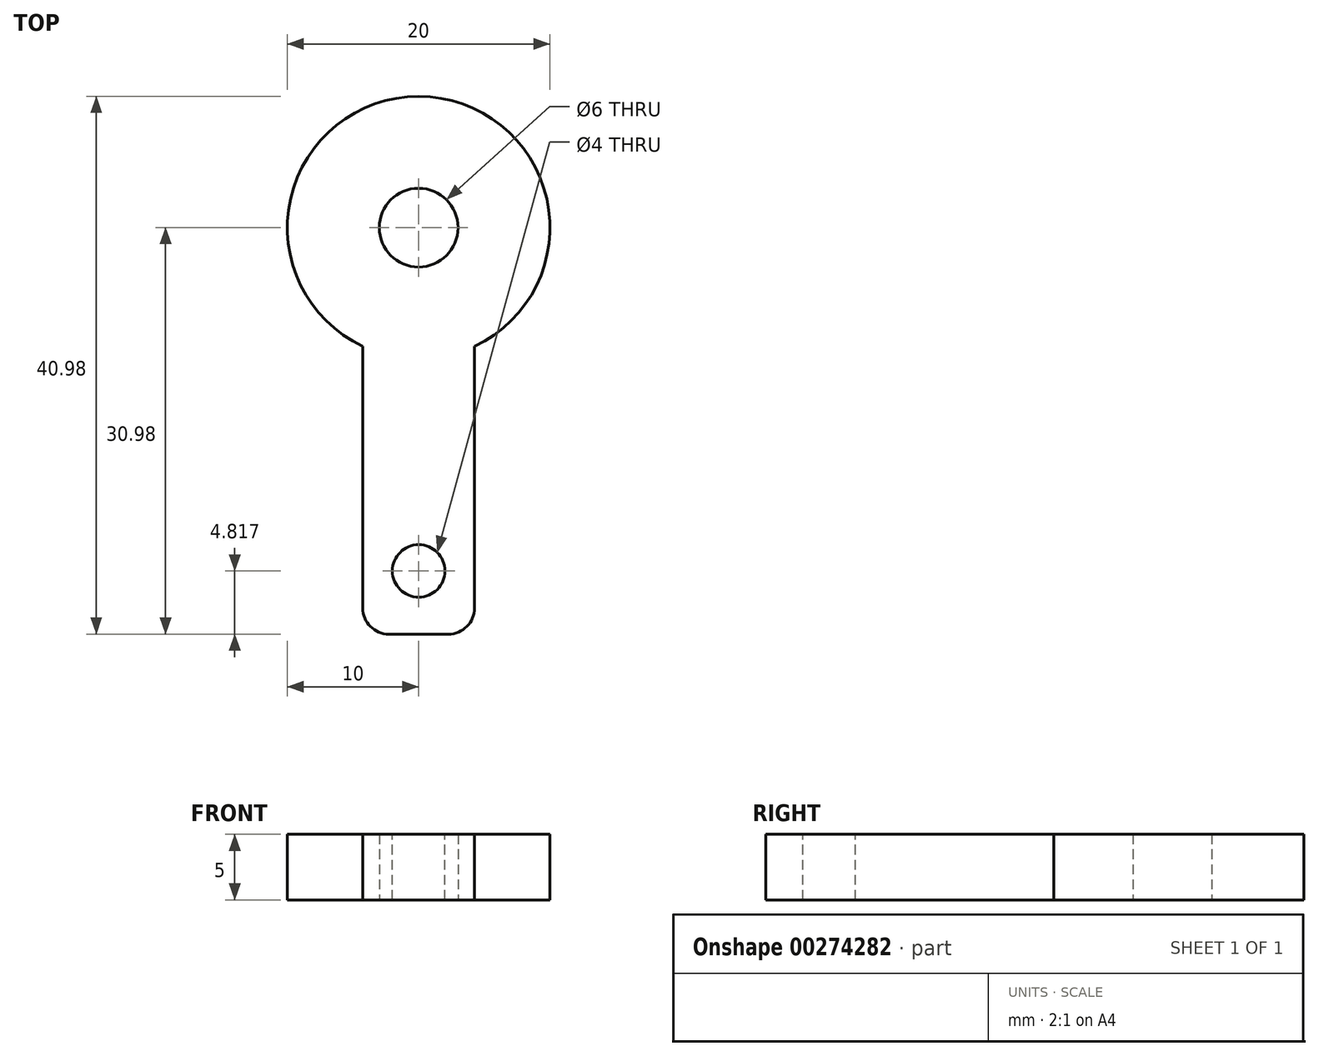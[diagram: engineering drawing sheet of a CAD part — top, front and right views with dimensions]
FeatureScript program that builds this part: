
annotation { "Feature Type Name" : "Feature", "Feature Type Description" : "" }
export const myFeature = defineFeature(function(context is Context, id is Id, definition is map)
    precondition{}
    {
        {
            var Q0;
            Q0=qCreatedBy(makeId("Top.planeOp"),FACE);
            var sketch = newSketch(context, id + "F0", { "sketchPlane" : qUnion([Q0])});
            skCircle(sketch, "E0", {"center": v(0, 0) * mm, "radius": 10 * mm});
            skCircle(sketch, "E1", {"center": v(0, 0) * mm, "radius": 3 * mm});
            skSolve(sketch);
        }
        {
            var Q0;
            Q0=makeQuery(id+"F0.imprint","IMPRINT",FACE,{"disambiguationData":[TD([[makeQuery(id+"F0.imprint","IMPRINT",EDGE,{"derivedFrom":sQuery(id+"F0.wireOp",EDGE,"E0")}),1.0]])]});
            extrude(context, id + "F1", {"entities" : qUnion([Q0]), "depth" : 5 * mm});
        }
        {
            var Q0;
            Q0=makeQuery(id+"F1.opExtrude","CAP_FACE",FACE,{"disambiguationData":[OSD([sQuery(id+"F0.wireOp",EDGE,"E0"),sQuery(id+"F0.wireOp",EDGE,"E1")])],"isStart":false});
            var sketch = newSketch(context, id + "F2", { "sketchPlane" : qUnion([Q0])});
            skCircle(sketch, "E2", {"center": v(0, 0) * mm, "radius": 4.26 * mm, "construction": true});
            skLineSegment(sketch, "E3.bottom", {"start": v(-4.26, 0) * mm, "end": v(4.26, 0) * mm});
            skLineSegment(sketch, "E3.top", {"start": v(-4.26, -30.98) * mm, "end": v(4.26, -30.98) * mm});
            skLineSegment(sketch, "E3.left", {"start": v(-4.26, 0) * mm, "end": v(-4.26, -30.98) * mm});
            skLineSegment(sketch, "E3.right", {"start": v(4.26, 0) * mm, "end": v(4.26, -30.98) * mm});
            skSolve(sketch);
        }
        {
            var Q0;
            {var subQ0=sQuery(id+"F2.wireOp",EDGE,"E3.top");Q0=makeQuery(id+"F2.imprint","IMPRINT",FACE,{"disambiguationData":[TD([[makeQuery(id+"F2.imprint","IMPRINT",EDGE,{"derivedFrom":subQ0}),1.0]])]});}
            extrude(context, id + "F3", {"entities" : qUnion([Q0]), "operationType" : NewBodyOperationType.ADD, "oppositeDirection" : true, "depth" : 5 * mm});
        }
        {
            var Q0;
            Q0=makeQuery(id+"F3.opExtrude","SWEPT_EDGE",EDGE,{"disambiguationData":[OSD([sQuery(id+"F2.wireOp",EDGE,"E3.top"),sQuery(id+"F2.wireOp",EDGE,"E3.left")])]});
            var Q1;
            Q1=makeQuery(id+"F3.opExtrude","SWEPT_EDGE",EDGE,{"disambiguationData":[OSD([sQuery(id+"F2.wireOp",EDGE,"E3.top"),sQuery(id+"F2.wireOp",EDGE,"E3.right")])]});
            fillet(context, id + "F4", {"entities" : qUnion([Q0, Q1]), "radius" : 2 * mm, "tangentPropagation" : true, "allowEdgeOverflow" : false});
        }
        {
            var Q0;
            {var subQ0=sQuery(id+"F0.wireOp",EDGE,"E0");Q0=makeQuery(id+"F3.boolean.opBoolean","MERGE",FACE,{"derivedFrom":[makeQuery(id+"F1.opExtrude","CAP_FACE",FACE,{"disambiguationData":[OSD([subQ0,sQuery(id+"F0.wireOp",EDGE,"E1")])],"isStart":false}),makeQuery(id+"F3.opExtrude","CAP_FACE",FACE,{"disambiguationData":[OSD([subQ0,sQuery(id+"F2.wireOp",EDGE,"E3.top"),sQuery(id+"F2.wireOp",EDGE,"E3.left"),sQuery(id+"F2.wireOp",EDGE,"E3.right")])],"isStart":true})]});}
            var sketch = newSketch(context, id + "F5", { "sketchPlane" : qUnion([Q0])});
            skCircle(sketch, "E4", {"center": v(0, -26.16) * mm, "radius": 2 * mm});
            skSolve(sketch);
        }
        {
            var Q0;
            Q0=makeQuery(id+"F5.imprint","IMPRINT",FACE,{"disambiguationData":[TD([[makeQuery(id+"F5.imprint","IMPRINT",EDGE,{"derivedFrom":sQuery(id+"F5.wireOp",EDGE,"E4")}),1.0]])]});
            extrude(context, id + "F6", {"entities" : qUnion([Q0]), "operationType" : NewBodyOperationType.REMOVE, "endBound" : BoundingType.THROUGH_ALL, "oppositeDirection" : true, "depth" : 25 * mm});
        }
    });
